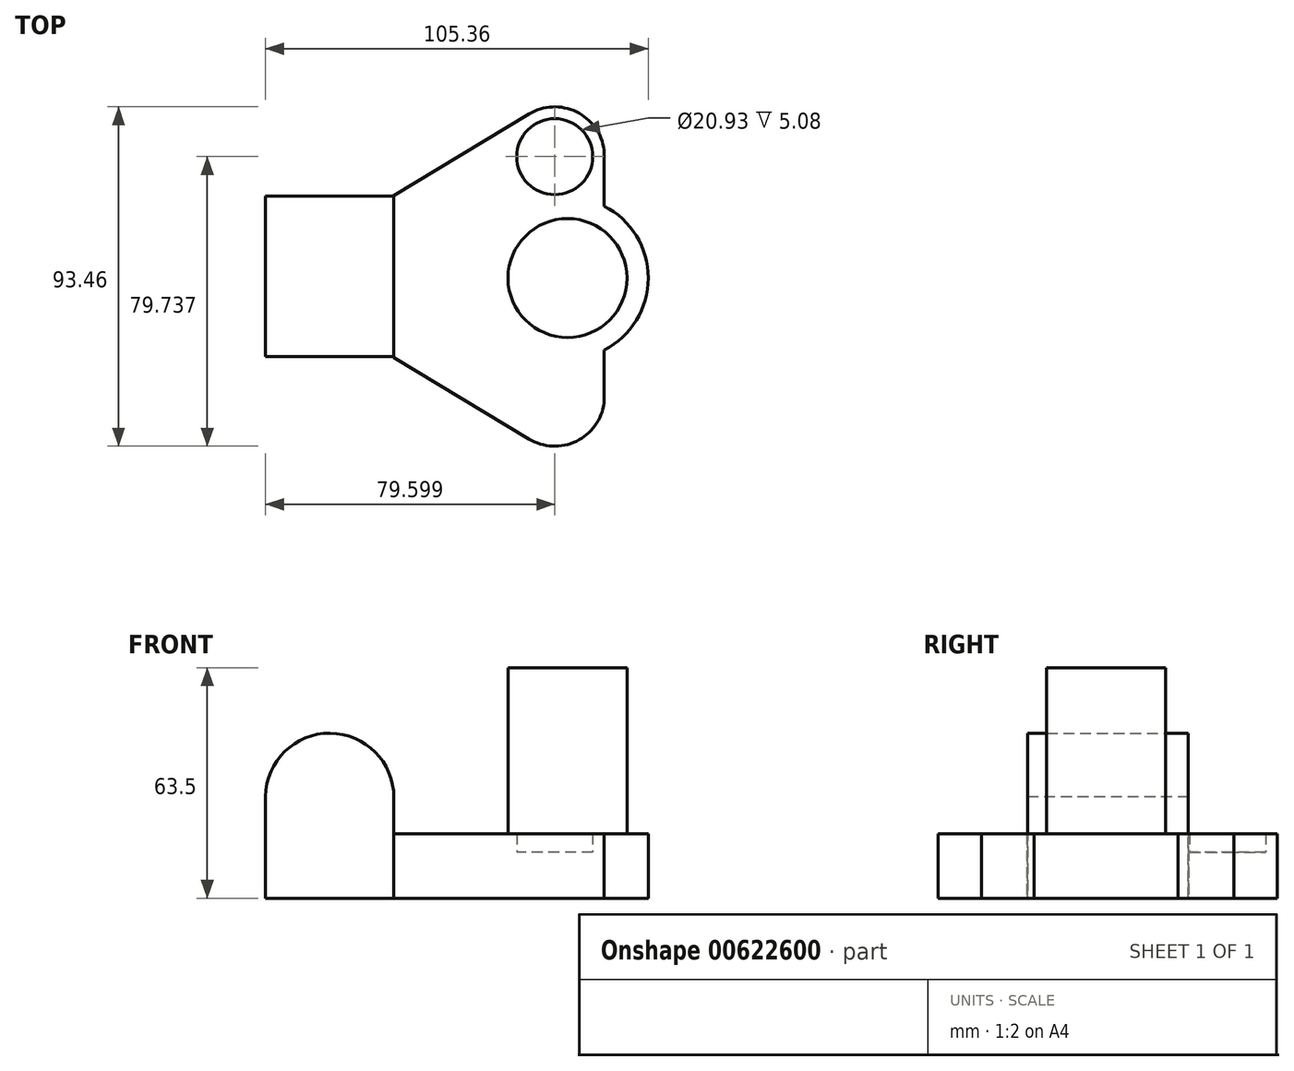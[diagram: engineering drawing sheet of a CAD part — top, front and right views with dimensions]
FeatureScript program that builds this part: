
annotation { "Feature Type Name" : "Feature", "Feature Type Description" : "" }
export const myFeature = defineFeature(function(context is Context, id is Id, definition is map)
    precondition{}
    {
        {
            var Q0;
            Q0=qCreatedBy(makeId("Top.planeOp"),FACE);
            var sketch = newSketch(context, id + "F0", { "sketchPlane" : qUnion([Q0])});
            skLineSegment(sketch, "E0", {"start": v(0, 22.24) * mm, "end": v(37.18, 44.75) * mm});
            skArc(sketch, "E1", {"start": v(37.18, 44.75) * mm, "mid": v(50.23, 45.37) * mm, "end": v(57.9, 34.8) * mm});
            skLineSegment(sketch, "E2", {"start": v(57.9, 34.8) * mm, "end": v(57.9, 19.4) * mm});
            skArc(sketch, "E3", {"start": v(57.9, -20.24) * mm, "mid": v(70.05, -0.42) * mm, "end": v(57.9, 19.4) * mm});
            skLineSegment(sketch, "E4.MirrorCS", {"start": v(0, -22.24) * mm, "end": v(37.18, -44.75) * mm});
            skArc(sketch, "E5.MirrorCS", {"start": v(37.18, -44.75) * mm, "mid": v(50.23, -45.37) * mm, "end": v(57.9, -34.8) * mm});
            skLineSegment(sketch, "E6.MirrorCS", {"start": v(57.9, -34.8) * mm, "end": v(57.9, -19.4) * mm});
            skLineSegment(sketch, "E7", {"start": v(0, -22.24) * mm, "end": v(0, 22.24) * mm});
            skSolve(sketch);
        }
        {
            var Q0;
            {var subQ1=sQuery(id+"F0.wireOp",EDGE,"E3");Q0=makeQuery(id+"F0.imprint","IMPRINT",FACE,{"disambiguationData":[TD([[makeQuery(id+"F0.imprint","IMPRINT",EDGE,{"derivedFrom":subQ1}),1.0]])]});}
            extrude(context, id + "F1", {"entities" : qUnion([Q0]), "depth" : 12.7 * mm, "offsetDistance" : 25.4 * mm});
        }
        {
            var Q0;
            Q0=qCreatedBy(makeId("Front.planeOp"),FACE);
            var sketch = newSketch(context, id + "F2", { "sketchPlane" : qUnion([Q0])});
            skLineSegment(sketch, "E8", {"start": v(0, 0) * mm, "end": v(0, 27.79) * mm});
            skArc(sketch, "E9", {"start": v(0, 27.79) * mm, "mid": v(-17.52, 45.44) * mm, "end": v(-35.3, 28.06) * mm});
            skLineSegment(sketch, "E10", {"start": v(-35.3, 28.06) * mm, "end": v(-35.3, 0) * mm});
            skLineSegment(sketch, "E11", {"start": v(-35.3, 0) * mm, "end": v(0, 0) * mm});
            skSolve(sketch);
        }
        {
            var Q0;
            Q0=makeQuery(id+"F2.imprint","IMPRINT",FACE,{"disambiguationData":[TD([[makeQuery(id+"F2.imprint","IMPRINT",EDGE,{"derivedFrom":sQuery(id+"F2.wireOp",EDGE,"E8")}),1.0]])]});
            extrude(context, id + "F3", {"entities" : qUnion([Q0]), "endBound" : BoundingType.SYMMETRIC, "depth" : 44.2 * mm, "offsetDistance" : 25.4 * mm});
        }
        {
            var Q0;
            Q0=makeQuery(id+"F1.opExtrude","CAP_FACE",FACE,{"disambiguationData":[OSD([sQuery(id+"F0.wireOp",EDGE,"E3"),sQuery(id+"F0.wireOp",EDGE,"E4.MirrorCS"),sQuery(id+"F0.wireOp",EDGE,"E5.MirrorCS"),sQuery(id+"F0.wireOp",EDGE,"E6.MirrorCS"),sQuery(id+"F0.wireOp",EDGE,"E2"),sQuery(id+"F0.wireOp",EDGE,"E1"),sQuery(id+"F0.wireOp",EDGE,"E0"),sQuery(id+"F0.wireOp",EDGE,"E7")])],"isStart":false});
            var sketch = newSketch(context, id + "F4", { "sketchPlane" : qUnion([Q0])});
            skCircle(sketch, "E12", {"center": v(47.8, -0.42) * mm, "radius": 16.36 * mm});
            skCircle(sketch, "E13", {"center": v(44.29, -33) * mm, "radius": 10.47 * mm});
            skCircle(sketch, "E14.MirrorC", {"center": v(44.29, 33) * mm, "radius": 10.47 * mm});
            skSolve(sketch);
        }
        {
            var Q0;
            Q0=makeQuery(id+"F4.imprint","IMPRINT",FACE,{"disambiguationData":[TD([[makeQuery(id+"F4.imprint","IMPRINT",EDGE,{"derivedFrom":sQuery(id+"F4.wireOp",EDGE,"E13")}),1.0]])]});
            var Q1;
            Q1=makeQuery(id+"F4.imprint","IMPRINT",FACE,{"disambiguationData":[TD([[makeQuery(id+"F4.imprint","IMPRINT",EDGE,{"derivedFrom":sQuery(id+"F4.wireOp",EDGE,"E14.MirrorC")}),-1.0]])]});
            extrude(context, id + "F5", {"entities" : qUnion([Q0, Q1]), "operationType" : NewBodyOperationType.ADD, "depth" : 5.08 * mm, "offsetDistance" : 25.4 * mm});
        }
        {
            var Q0;
            Q0=makeQuery(id+"F4.imprint","IMPRINT",FACE,{"disambiguationData":[TD([[makeQuery(id+"F4.imprint","IMPRINT",EDGE,{"derivedFrom":sQuery(id+"F4.wireOp",EDGE,"E12")}),1.0]])]});
            extrude(context, id + "F6", {"entities" : qUnion([Q0]), "operationType" : NewBodyOperationType.ADD, "depth" : 50.8 * mm, "offsetDistance" : 25.4 * mm});
        }
    });
